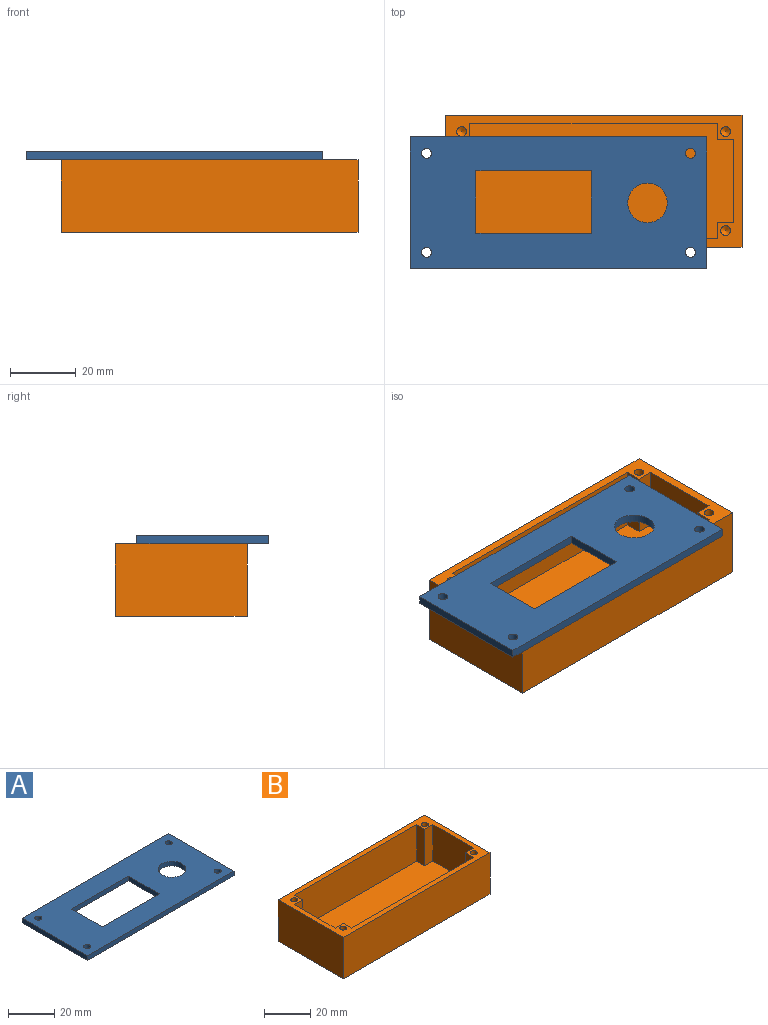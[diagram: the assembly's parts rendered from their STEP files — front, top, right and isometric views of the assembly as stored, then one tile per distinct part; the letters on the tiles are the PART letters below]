
ASSEMBLY  parts=2 mates=1
PART A: 15 faces, bbox 90x40x2.5 mm
  f0: plane 40x2.5mm, normal (-1,0,0), area 100mm2, adj f1,f11,f12,f13
  f1: plane 90x2.5mm, normal (0,-1,0), area 225mm2, adj f0,f2,f12,f13
  f2: plane 40x2.5mm, normal (1,0,0), area 100mm2, adj f1,f11,f12,f13
  f3: plane 35x2.5mm, normal (0,-1,0), area 87.5mm2, adj f4,f6,f12,f13
  f4: plane 19x2.5mm, normal (-1,0,0), area 47.5mm2, adj f3,f5,f12,f13
  f5: plane 35x2.5mm, normal (0,1,0), area 87.5mm2, adj f4,f6,f12,f13
  f6: plane 19x2.5mm, normal (1,0,0), area 47.5mm2, adj f3,f5,f12,f13
  f7: cylinder r=1.5mm len=3mm, axis (0,0,-1), area 23.6mm2, adj f12,f13
  f8: cylinder r=1.5mm len=3mm, axis (0,0,-1), area 23.6mm2, adj f12,f13
  f9: cylinder r=1.5mm len=3mm, axis (0,0,-1), area 23.6mm2, adj f12,f13
  f10: cylinder r=1.5mm len=3mm, axis (0,0,-1), area 23.6mm2, adj f12,f13
  f11: plane 90x2.5mm, normal (0,1,0), area 225mm2, adj f0,f2,f12,f13
  f12: plane 90x40mm, normal (0,0,1), area 2793.6mm2, adj f0,f1,f2,f3,f4,f5,f6,f7
  f13: plane 90x40mm, normal (0,0,-1), area 2793.6mm2, adj f0,f1,f2,f3,f4,f5,f6,f7
  f14: cylinder r=6mm len=12mm, axis (0,0,-1), area 94.2mm2, adj f12,f13
PART B: 27 faces, bbox 90x40x22 mm
  f0: plane 85x35mm, normal (0,0,1), area 2875mm2, adj f1,f2,f3,f4,f11,f12,f13,f14
  f1: plane 25x19.5mm, normal (-1,0,0), area 487.5mm2, adj f0,f9,f16,f18
  f2: plane 75x19.5mm, normal (0,1,0), area 1462.5mm2, adj f0,f9,f13,f17
  f3: plane 25x19.5mm, normal (1,0,0), area 487.5mm2, adj f0,f9,f11,f14
  f4: plane 75x19.5mm, normal (0,-1,0), area 1462.5mm2, adj f0,f9,f12,f15
  f5: plane 40x22mm, normal (-1,0,0), area 880mm2, adj f6,f8,f9,f10
  f6: plane 90x22mm, normal (0,-1,0), area 1980mm2, adj f5,f7,f9,f10
  f7: plane 40x22mm, normal (1,0,0), area 880mm2, adj f6,f8,f9,f10
  f8: plane 90x22mm, normal (0,1,0), area 1980mm2, adj f5,f7,f9,f10
  f9: plane 90x40mm, normal (0,0,1), area 696.7mm2, adj f1,f2,f3,f4,f5,f6,f7,f8
  f10: plane 90x40mm, normal (0,0,-1), area 3600mm2, adj f5,f6,f7,f8
  f11: plane 19.5x5mm, normal (0,-1,0), area 97.5mm2, adj f0,f3,f9,f12
  f12: plane 19.5x5mm, normal (1,0,0), area 97.5mm2, adj f0,f4,f9,f11
  f13: plane 19.5x5mm, normal (1,0,0), area 97.5mm2, adj f0,f2,f9,f14
  f14: plane 19.5x5mm, normal (0,1,0), area 97.5mm2, adj f0,f3,f9,f13
  f15: plane 19.5x5mm, normal (-1,0,0), area 97.5mm2, adj f0,f4,f9,f16
  f16: plane 19.5x5mm, normal (0,-1,0), area 97.5mm2, adj f0,f1,f9,f15
  f17: plane 19.5x5mm, normal (-1,0,0), area 97.5mm2, adj f0,f2,f9,f18
  f18: plane 19.5x5mm, normal (0,1,0), area 97.5mm2, adj f0,f1,f9,f17
  f19: cylinder r=1.5mm len=15mm, axis (0,0,1), area 141.4mm2, adj f9,f20
  f20: cone r=0mm half-angle=59deg, axis (0,0,1), area 8.2mm2, adj f19
  f21: cylinder r=1.5mm len=15mm, axis (0,0,1), area 141.4mm2, adj f9,f22
  f22: cone r=0mm half-angle=59deg, axis (0,0,1), area 8.2mm2, adj f21
  f23: cylinder r=1.5mm len=15mm, axis (0,0,1), area 141.4mm2, adj f9,f24
  f24: cone r=0mm half-angle=59deg, axis (0,0,1), area 8.2mm2, adj f23
  f25: cylinder r=1.5mm len=15mm, axis (0,0,1), area 141.4mm2, adj f9,f26
  f26: cone r=0mm half-angle=59deg, axis (0,0,1), area 8.2mm2, adj f25
PLACE A t=(-80.09,-7.5,-28.8)mm
PLACE B t=(73.9,-83.24,-50.8)mm
MATE planar B.f9 <-> A.f13  axis (0,0,1) through (-22.9,19.8,-28.8)mm
